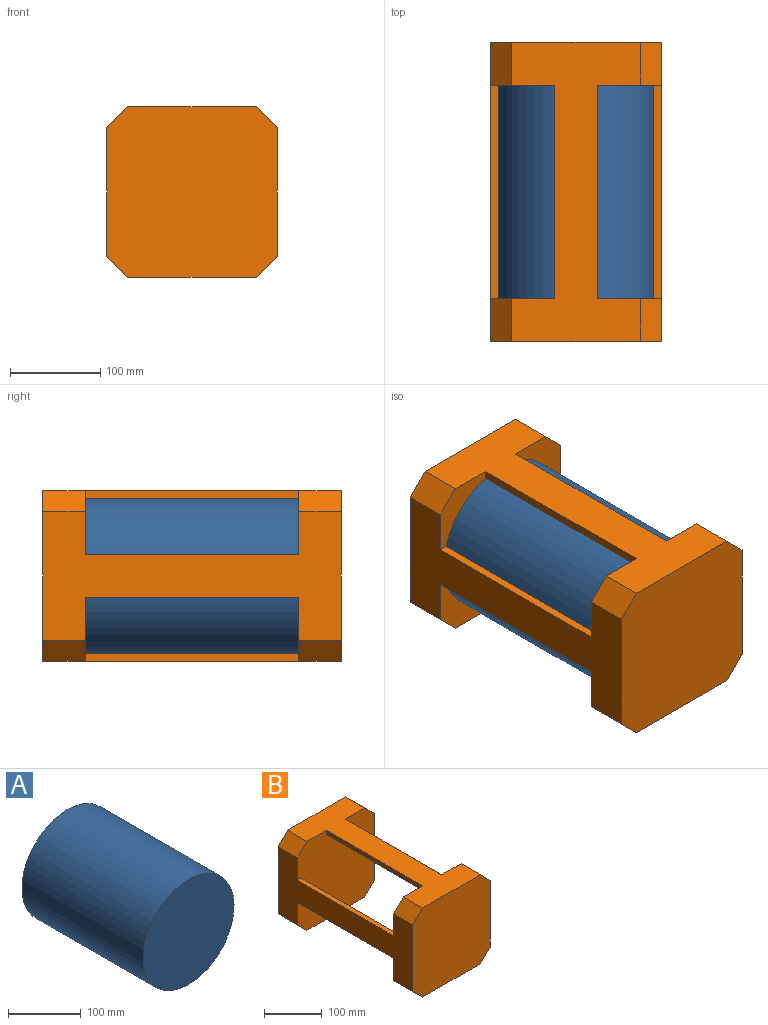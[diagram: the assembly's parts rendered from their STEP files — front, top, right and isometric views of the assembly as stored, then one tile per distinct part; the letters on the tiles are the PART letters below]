
ASSEMBLY  parts=2 mates=1
PART A: 3 faces, bbox 176.9x235.9x176.9 mm
  f0: cylinder r=88.45mm len=235.86mm, axis (0,-1,0), area 131071.8mm2, adj f1,f2
  f1: plane 176.89x176.89mm, normal (0,1,0), area 24576mm2, adj f0
  f2: plane 176.89x176.89mm, normal (0,-1,0), area 24576mm2, adj f0
PART B: 28 faces, bbox 188.7x330.2x188.7 mm
  f0: plane 188.69x188.69mm, normal (0,1,0), area 33177.2mm2, adj f1,f2,f3,f4,f5,f6,f7,f8
  f1: plane 330.2x141.51mm, normal (0,0,-1), area 24476.6mm2, adj f0,f2,f8,f9,f13,f14,f22,f23
  f2: plane 47.17x23.59mm, normal (0.71,0,-0.71), area 1573.4mm2, adj f0,f1,f3,f9
  f3: plane 330.2x141.51mm, normal (1,0,0), area 24476.6mm2, adj f0,f2,f4,f9,f19,f21,f22,f23
  f4: plane 47.17x23.59mm, normal (0.71,0,0.71), area 1573.4mm2, adj f0,f3,f5,f9
  f5: plane 330.2x141.51mm, normal (0,0,1), area 24476.6mm2, adj f0,f4,f6,f9,f10,f12,f22,f24
  f6: plane 47.17x23.59mm, normal (-0.71,0,0.71), area 1573.4mm2, adj f0,f5,f7,f9
  f7: plane 330.2x141.51mm, normal (-1,0,0), area 24476.6mm2, adj f0,f6,f8,f9,f17,f18,f22,f25
  f8: plane 47.17x23.59mm, normal (-0.71,0,-0.71), area 1573.4mm2, adj f0,f1,f7,f9
  f9: plane 188.69x188.69mm, normal (0,-1,0), area 34489.7mm2, adj f1,f2,f3,f4,f5,f6,f7,f8
  f10: plane 235.86x9.1mm, normal (-1,0,0), area 2146.1mm2, adj f0,f5,f11,f22
  f11: cylinder r=88.45mm len=235.86mm, axis (0,-1,0), area 11262mm2, adj f0,f10,f12,f22
  f12: plane 235.86x9.1mm, normal (1,0,0), area 2146.1mm2, adj f0,f5,f11,f22
  f13: plane 235.86x9.1mm, normal (-1,0,0), area 2146.1mm2, adj f0,f1,f15,f22
  f14: plane 235.86x9.1mm, normal (1,0,0), area 2146.1mm2, adj f0,f1,f15,f22
  f15: cylinder r=88.45mm len=235.86mm, axis (0,-1,0), area 11262mm2, adj f0,f13,f14,f22
  f16: cylinder r=88.45mm len=235.86mm, axis (0,-1,0), area 11262mm2, adj f0,f17,f18,f22
  f17: plane 235.86x9.1mm, normal (0,0,1), area 2146.1mm2, adj f0,f7,f16,f22
  f18: plane 235.86x9.1mm, normal (0,0,-1), area 2146.1mm2, adj f0,f7,f16,f22
  f19: plane 235.86x9.1mm, normal (0,0,1), area 2146.1mm2, adj f0,f3,f20,f22
  f20: cylinder r=88.45mm len=235.86mm, axis (0,-1,0), area 11262mm2, adj f0,f19,f21,f22
  f21: plane 235.86x9.1mm, normal (0,0,-1), area 2146.1mm2, adj f0,f3,f20,f22
  f22: plane 188.69x188.69mm, normal (0,-1,0), area 33177.2mm2, adj f1,f3,f5,f7,f10,f11,f12,f13
  f23: plane 47.17x23.59mm, normal (0.71,0,-0.71), area 1573.4mm2, adj f1,f3,f22,f27
  f24: plane 47.17x23.59mm, normal (0.71,0,0.71), area 1573.4mm2, adj f3,f5,f22,f27
  f25: plane 47.17x23.59mm, normal (-0.71,0,0.71), area 1573.4mm2, adj f5,f7,f22,f27
  f26: plane 47.17x23.59mm, normal (-0.71,0,-0.71), area 1573.4mm2, adj f1,f7,f22,f27
  f27: plane 188.69x188.69mm, normal (0,1,0), area 34489.7mm2, adj f1,f3,f5,f7,f23,f24,f25,f26
PLACE A t=(471.36,-381.84,-4.73)mm
PLACE B t=(4,-381.84,-4.73)mm
MATE fastened A.f0 <-> B.f20  axis (0,-1,0) through (4,108.01,-4.73)mm
